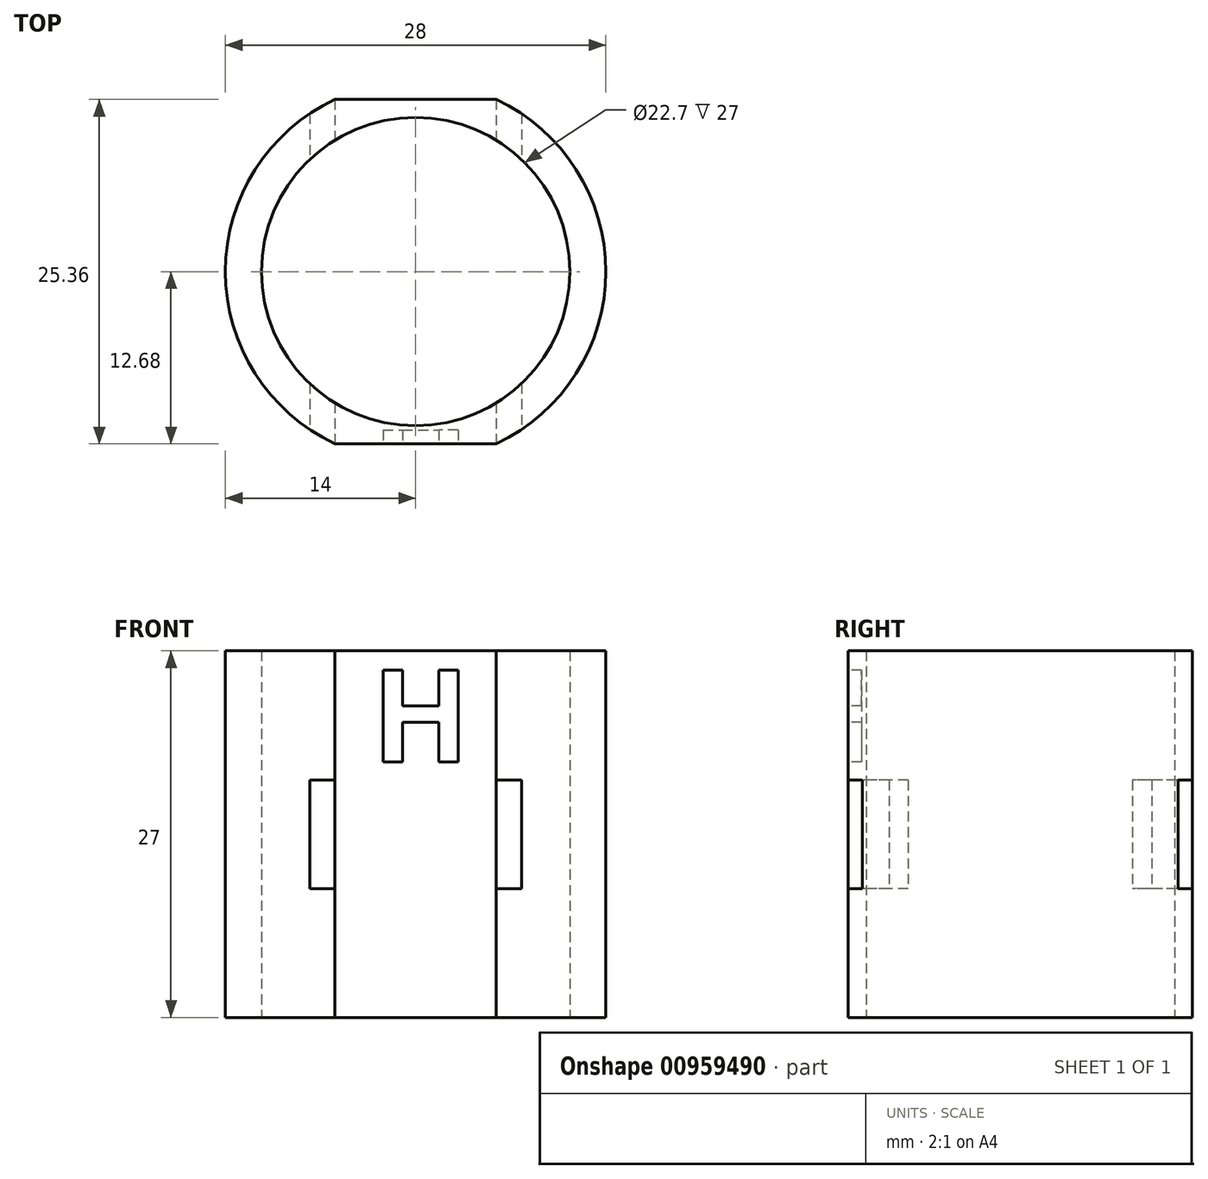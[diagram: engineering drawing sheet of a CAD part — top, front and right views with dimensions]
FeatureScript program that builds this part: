
annotation { "Feature Type Name" : "Feature", "Feature Type Description" : "" }
export const myFeature = defineFeature(function(context is Context, id is Id, definition is map)
    precondition{}
    {
        {
            var Q0;
            Q0=qCreatedBy(makeId("Top.planeOp"),FACE);
            var sketch = newSketch(context, id + "F0", { "sketchPlane" : qUnion([Q0])});
            skCircle(sketch, "E0", {"center": v(0, 0) * mm, "radius": 14 * mm});
            skCircle(sketch, "E1", {"center": v(0, 0) * mm, "radius": 11.35 * mm});
            skLineSegment(sketch, "E2", {"start": v(0, 0) * mm, "end": v(0, 11.35) * mm});
            skLineSegment(sketch, "E3", {"start": v(0, 0) * mm, "end": v(14, 0) * mm});
            skLineSegment(sketch, "E4", {"start": v(0, 11.35) * mm, "end": v(-8.2, 11.35) * mm});
            skLineSegment(sketch, "E5", {"start": v(0, 11.35) * mm, "end": v(0, 14) * mm});
            skLineSegment(sketch, "E6", {"start": v(0, 12.68) * mm, "end": v(-5.95, 12.68) * mm});
            skLineSegment(sketch, "E7", {"start": v(-5.95, 12.68) * mm, "end": v(5.95, 12.68) * mm});
            skLineSegment(sketch, "E8.MirrorCS", {"start": v(-5.95, -12.68) * mm, "end": v(5.95, -12.68) * mm});
            skSolve(sketch);
        }
        {
            var Q0;
            {var subQ0=sQuery(id+"F0.wireOp",EDGE,"E4");Q0=makeQuery(id+"F0.imprint","IMPRINT",FACE,{"disambiguationData":[TD([[makeQuery(id+"F0.imprint","IMPRINT",EDGE,{"derivedFrom":subQ0}),1.0]])]});}
            var Q1;
            {var subQ5=sQuery(id+"F0.wireOp",EDGE,"E3");var subQ6=sQuery(id+"F0.wireOp",EDGE,"E0");var subQ7=makeQuery(id+"F0.imprint","INTERSECT",VERTEX,{"derivedFrom":[subQ6,subQ5]});Q1=makeQuery(id+"F0.imprint","IMPRINT",FACE,{"disambiguationData":[TD([[makeQuery(id+"F0.imprint","IMPRINT",EDGE,{"disambiguationData":[TD([[subQ7,-1.0]])],"derivedFrom":subQ6}),1.0]])]});}
            var Q2;
            {var subQ0=sQuery(id+"F0.wireOp",EDGE,"E4");Q2=makeQuery(id+"F0.imprint","IMPRINT",FACE,{"disambiguationData":[TD([[makeQuery(id+"F0.imprint","IMPRINT",EDGE,{"derivedFrom":subQ0}),-1.0]])]});}
            extrude(context, id + "F1", {"entities" : qUnion([Q0, Q1, Q2]), "depth" : 27 * mm, "offsetDistance" : 25 * mm});
        }
        {
            var Q0;
            Q0=makeQuery(id+"F1.opExtrude","SWEPT_FACE",FACE,{"disambiguationData":[OSD([sQuery(id+"F0.wireOp",EDGE,"E8.MirrorCS")])]});
            var sketch = newSketch(context, id + "F2", { "sketchPlane" : qUnion([Q0])});
            skLineSegment(sketch, "E9", {"start": v(0, 27) * mm, "end": v(0, 0) * mm});
            skLineSegment(sketch, "E10", {"start": v(-5.95, 9.47) * mm, "end": v(5.95, 9.47) * mm});
            skLineSegment(sketch, "E11", {"start": v(0, 9.47) * mm, "end": v(7.8, 9.47) * mm});
            skLineSegment(sketch, "E12", {"start": v(0, 9.47) * mm, "end": v(-7.8, 9.47) * mm});
            skLineSegment(sketch, "E13", {"start": v(7.8, 9.47) * mm, "end": v(7.8, 17.47) * mm});
            skLineSegment(sketch, "E14", {"start": v(-1.98, 17.5) * mm, "end": v(-1.98, 27) * mm});
            skLineSegment(sketch, "E15", {"start": v(-1.82, 9.47) * mm, "end": v(-1.82, 0) * mm});
            skLineSegment(sketch, "E16", {"start": v(-7.8, 9.47) * mm, "end": v(-7.8, 17.47) * mm});
            skLineSegment(sketch, "E17", {"start": v(-7.8, 17.47) * mm, "end": v(7.8, 17.47) * mm});
            skSolve(sketch);
        }
        {
            var Q0;
            {var subQ0=sQuery(id+"F2.wireOp",EDGE,"E12");Q0=makeQuery(id+"F2.imprint","IMPRINT",FACE,{"disambiguationData":[TD([[makeQuery(id+"F2.imprint","IMPRINT",EDGE,{"derivedFrom":subQ0}),-1.0]])]});}
            var Q1;
            {var subQ0=sQuery(id+"F2.wireOp",EDGE,"E11");Q1=makeQuery(id+"F2.imprint","IMPRINT",FACE,{"disambiguationData":[TD([[makeQuery(id+"F2.imprint","IMPRINT",EDGE,{"derivedFrom":subQ0}),1.0]])]});}
            var Q2;
            {var subQ0=sQuery(id+"F2.wireOp",EDGE,"UeriPeqR-QFXt-dTMW-cwMM-hMRWZIPTNx4J");Q2=makeQuery(id+"F2.imprint","IMPRINT",FACE,{"disambiguationData":[TD([[makeQuery(id+"F2.imprint","IMPRINT",EDGE,{"derivedFrom":subQ0}),1.0]])]});}
            var Q3;
            {var subQ0=sQuery(id+"F2.wireOp",EDGE,"E16");Q3=makeQuery(id+"F2.imprint","IMPRINT",FACE,{"disambiguationData":[TD([[makeQuery(id+"F2.imprint","IMPRINT",EDGE,{"derivedFrom":subQ0}),-1.0]])]});}
            extrude(context, id + "F3", {"entities" : qUnion([Q0, Q1, Q2, Q3]), "operationType" : NewBodyOperationType.REMOVE, "oppositeDirection" : true, "depth" : 37.2 * mm, "offsetDistance" : 25 * mm});
        }
        {
            var Q0;
            {var subQ0=sQuery(id+"F0.wireOp",EDGE,"E8.MirrorCS");Q0=makeQuery(id+"F3.boolean.opBoolean","SPLIT",FACE,{"disambiguationData":[TD([makeQuery(id+"F3.opExtrude","SWEPT_FACE",FACE,{"disambiguationData":[OSD([sQuery(id+"F2.wireOp",EDGE,"E17")])]})])],"derivedFrom":makeQuery(id+"F1.opExtrude","SWEPT_FACE",FACE,{"disambiguationData":[OSD([subQ0])]})});}
            var sketch = newSketch(context, id + "F4", { "sketchPlane" : qUnion([Q0])});
            skText(sketch, "E18", { "text": "H", "fontName": "NotoSans-Bold.ttf"});
            const initialGuessF4  = {"E18": [-0.00325, 0.01883, 1, 0, 0.00681]};
            skSetInitialGuess(sketch, initialGuessF4);
            skSolve(sketch);
        }
        {
            var Q0;
            Q0=makeQuery(id+"F4.imprint","IMPRINT",FACE,{"disambiguationData":[TD([[makeQuery(id+"F4.imprint","IMPRINT",EDGE,{"derivedFrom":sQuery(id+"F4.wireOp",EDGE,"E18.sketch_text.stroke-0")}),-1.0]])]});
            extrude(context, id + "F5", {"entities" : qUnion([Q0]), "operationType" : NewBodyOperationType.REMOVE, "oppositeDirection" : true, "depth" : 1 * mm, "offsetDistance" : 25 * mm});
        }
    });
